# Revit family: Thorn IQ-WAVE
name_source: partatom
category: Lighting Fixtures
revit_build: Autodesk Revit 2016 (Build: 20150220_1215(x64)
units: mm (PartAtom-declared; Revit-internal decimal feet)

## family parameters
Cut with Voids When Loaded = No
Host = Face
Light Source = Yes
Part Type = Normal
Room Calculation Point = No
Round Connector Dimension = Use Diameter
Shared = No

## types (6) — shared parameters
Body Material = Thorn White Polycarbonate
Color Filter = 16777215
Dimming Lamp Color Temperature Shift = <None>
Emit Shape Visible in Rendering = No
Emit from Rectangle Length = 210 mm  [stored 0.688976 ft]
Height = 70 mm  [stored 0.229659 ft]
Manufacturer = Thorn Lighting
Suspension Material = Thorn White Polycarbonate
Tilt Angle = -90.00°
Width = 210 mm  [stored 0.688976 ft]
zero-valued in all types: Cost, Default Elevation

## per-type parameters (varying)
| type | Apparent Load | Emit from Rectangle Width | Length | Model | Photometric Web File | URL |
| IQ-Wave INFILL 385 | 0 VA | 385 mm  [stored 1.26312 ft] | 385 mm  [stored 1.26312 ft] | 96629772 | generic | www.thornlighting.com/96629772 |
| IQ-Wave INFILL 565 | 0 VA | 565 mm  [stored 1.85367 ft] | 565 mm  [stored 1.85367 ft] | 96629773 | generic | www.thornlighting.com/96629773 |
| IQ-Wave INFILL 954 | 0 VA | 954 mm  [stored 3.12992 ft] | 954 mm  [stored 3.12992 ft] | 96629774 | generic | www.thornlighting.com/96629774 |
| IQ-Wave INFILL 1131 | 0 VA | 1131 mm  [stored 3.71063 ft] | 1131 mm  [stored 3.71063 ft] | 96629775 | generic | www.thornlighting.com/96629775 |
| IQ SURF L LED4900-840 HFIX | 42 VA | 1440 mm  [stored 4.72441 ft] | 1440 mm  [stored 4.72441 ft] | 96628947 | 96628947_(STD).IES | www.thornlighting.com/96628947 |
| IQ SUSP S LED4900-840 HFIX ML5 | 42 VA | 1140 mm  [stored 3.74016 ft] | 1140 mm  [stored 3.74016 ft] | 96628955 | 96628955_(STD).IES | www.thornlighting.com/96628955 |

note: [stored X ft] marks values corroborated as IEEE doubles in the binary element streams (Revit-internal decimal feet)

## geometry (parser evidence)
native form markers: Blend x15, Sweep x4
no freeform markers — native parametric forms only
